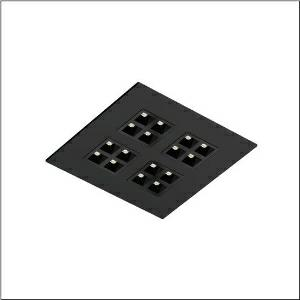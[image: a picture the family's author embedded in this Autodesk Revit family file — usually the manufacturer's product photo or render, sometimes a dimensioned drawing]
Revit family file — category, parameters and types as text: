
# Revit family: silica_31_square_51my6lmu44ba
name_source: partatom
category: Lighting Fixtures
units: mm (PartAtom-declared; Revit-internal decimal feet)

## family parameters
Cut with Voids When Loaded = No
Host = Face
Light Source = No
Part Type = Normal
Room Calculation Point = No
Round Connector Dimension = Use Diameter
Shared = No

## types (1)
- --- (1 x LED, 6620 lm, 39 W, 4000K)
    Apparent Load = 39 VA
    CIE Flux Codes = 82 100 100 100 100
    Color Rendering = 80
    Color Temperature = 4000K
    Default Elevation = 1800 mm
    Description = Silica 31 Square, office luminaire, primary light control with lens, of PMMA, primary anti-glare with reflector, of PC, black, light emission: direct distribution, primary light characteristic: symmetric, installation type: lay-in mounting, LED, rated luminous flux: 4.610lm, luminous efficacy: 177lm/W, light colour: 840, colour temperature: 4000K, control gear: ON/OFF Multilumen, with terminal, 3-pole, mains connection: 220..240V, AC, 50/60Hz, rated input power: 26W, luminaire housing, of sheet steel, coated, jet black (RAL 9005), module: M625, length: 620mm, width: 620mm, height: 43mm, protection rating (complete): IP20, insulation class (complete): insulation class II (safety insulation), certification: CE, impact resistance: IK03, permissible operating ambient temperature: -20..+35°C, standard: EN 50419, packaging unit: 1 piece
    Height = 0 mm  [stored 0 ft]
    Lamp = 1 x LED
    Lamp Light Flux = 6620 lm
    Lamp Power = 39 W
    Lamp count = 1
    Length = 620 mm
    Luminous efficacy = 170 lm/W
    Manufacturer = Siteco
    ModVariant = No
    Model = 51MY6LMU44BA
    Mounting Place = Ceiling
    Mounting Type = Recessed
    Number of Poles = 1
    OnlyDefault = Yes
    Power Factor = 1
    Product Name = Silica 31 Square
    Product group = office luminaire | ceiling recessed
    ProductGroupID = 400
    Protection Class = Protection class II
    Protection Degree = IP 20
    RLX_Detail_Level = 1
    RLX_Emergency_Light_Flux = 0 lm
    RLX_Emergency_Type = 0
    RLX_Emergency_Type_DB = No
    RlxData = <blob elided: 36329 chars, md5=542ce7b7>
    Socket = socket
    Standby Power = 0 W
    System Light Flux = 6620 lm
    System Power = 39 W
    Type Comments = factory setting: luminous flux: 100 % | (ON | ON | ON | ON) | 1100 mA
    Type Image = l_1313660.jpg
    URL = http://relux.com
    VarID = @adj_043341
    Voltage = 0 V
    Weight = 0.00 kg
    Width = 620 mm

note: [stored X ft] marks values corroborated as IEEE doubles in the binary element streams (Revit-internal decimal feet)

## geometry (parser evidence)
native form markers: Blend x4, Sweep x11
no freeform markers — native parametric forms only
